# Revit family: NBS_TapcoRoofingProducts_DryFxngHips_HipMaster
name_source: partatom
category: Generic Models
units: mm (PartAtom-declared; Revit-internal decimal feet)

## family parameters
Can host rebar = No
Cut with Voids When Loaded = No
Part Type = Normal
Room Calculation Point = No
Round Connector Dimension = Use Diameter
Shared = No

## types (1)
- HipMaster
    Applications = Suitable for use with the TapcoSlate Classic Ridge/ Hip system, for roof pitches 14 to 45 degrees
    AssetType = Fixed
    BIMObjectName = NBS_TapcoRoofingProducts_DryFixingHips_HipMaster
    Category = Pr_35_90_93_28:Dry fixing hips
    Color = Black
    Combustible = Yes
    Description = A dry-fix hip ventilation system that fits underneath the TapcoSlate Classic Ridge/ Hip system
    DurationUnit = year
    ExpectedLife = 50+ years
    Features = Enhanced roof ventilation at the hip, patented triple-baffle system engineered to keep blowing rain and snow from getting in, internal filter blocks out insects, leaves and other debris, the low-profile design is unobtrusive, nailing supports and structural ribs make the Hip Master crushproof, to withstand falling tree branches and hammer blows, and it resists cracking, self-aligning, interlocking ends make it easy to install correctly, built-in end caps adjust to the roof pitch while the ship-lap design allows for expansion and contraction as temperatures change, can be joined with Ridge Master Plus ridge ventilation, 10 000 mm²/m ventilation provision to comply with building regulations for both warm and cold roofs
    IfcExportAs = IfcCoveringType
    IfcExportType = ROOFING
    IsExternal = Yes
    ManufacturerName = Tapco Roofing Products
    ManufacturerURL = www.tapcoroofingproducts.com
    Material = Polypropylene (PP) and Rubber
    ModelReference = HipMaster
    NBSCertification = www.nationalbimlibrary.com/cert/0lh4n1mo
    NBSDescription = Dry fixing hips
    NBSReference = 45-80-90/374
    Name = DryFixingHips_HipMaster_TapcoRoofingProducts
    NominalHeight = 35 mm  [stored 0.114829 ft]
    NominalLength = 1219 mm
    NominalWidth = 270 mm
    PitchRange = 14° - 45°
    ProductInformation = https://www.tapcoroofingproducts.com
    RidgeMaterial = NBS_TapcoRoofingProducts_Polypropylene_Black
    Size = 1219 x 270 x 35 mm
    Status = UNSET
    ThermalTransmittance = 0
    Uniclass2015Code = Pr_35_90_93_28
    Uniclass2015Title = Dry fixing hips
    Uniclass2015Version = Products v1.20
    Version = 1
    WarrantyDescription = 40-years
    WarrantyDurationUnit = year

note: [stored X ft] marks values corroborated as IEEE doubles in the binary element streams (Revit-internal decimal feet)

## geometry (parser evidence)
native form markers: Sweep x3
no freeform markers — native parametric forms only
